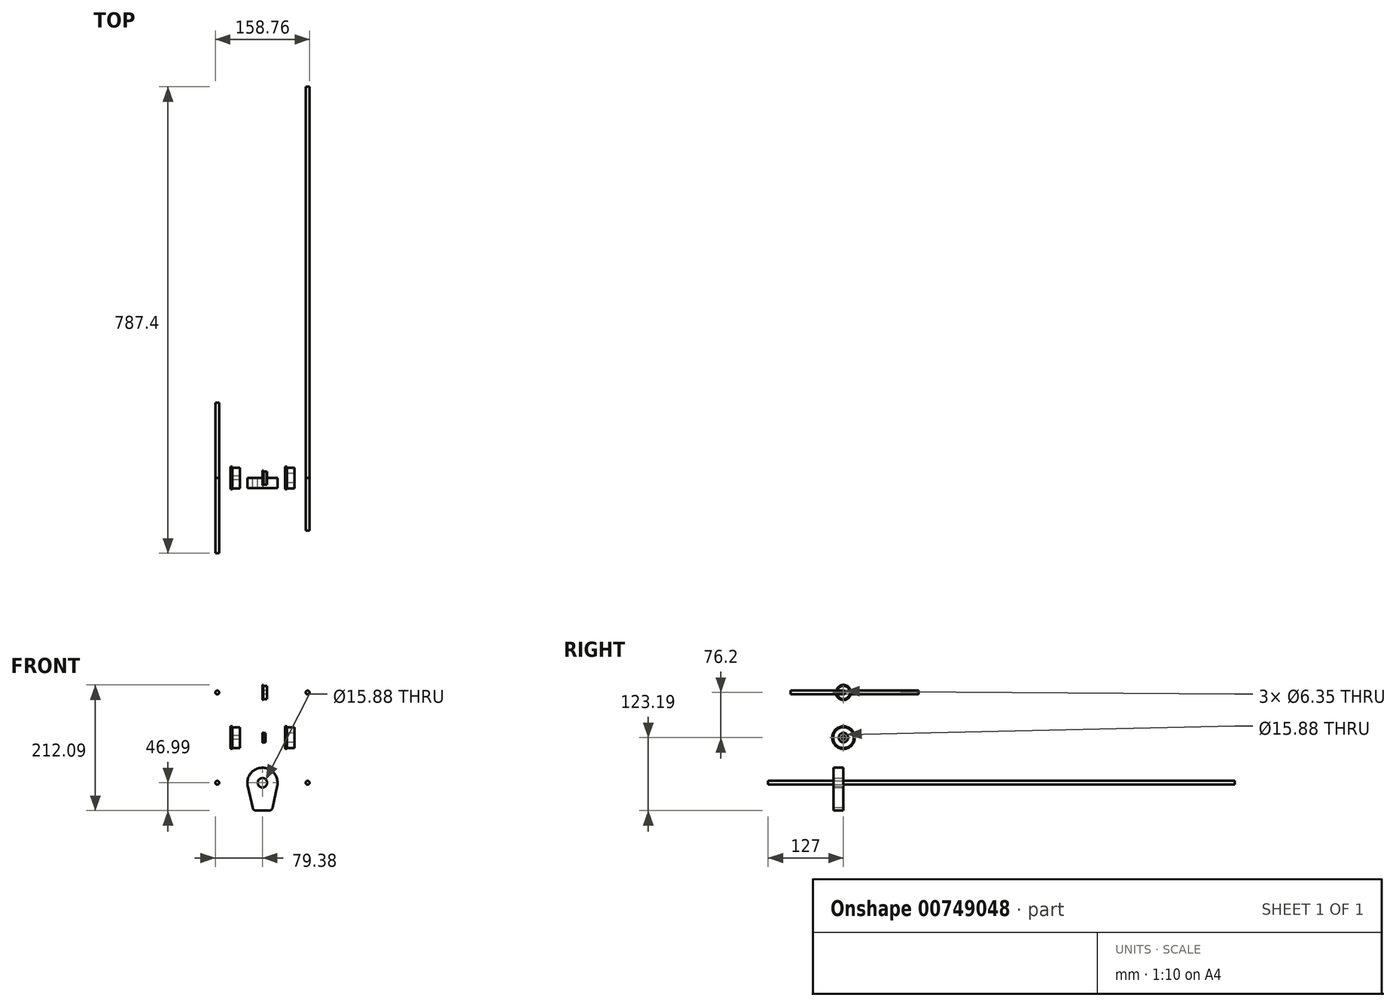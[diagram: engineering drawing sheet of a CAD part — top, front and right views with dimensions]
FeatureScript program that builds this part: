
annotation { "Feature Type Name" : "Feature", "Feature Type Description" : "" }
export const myFeature = defineFeature(function(context is Context, id is Id, definition is map)
    precondition{}
    {
        {
            var Q0;
            Q0=qCreatedBy(makeId("Front.planeOp"),FACE);
            var sketch = newSketch(context, id + "F0", { "sketchPlane" : qUnion([Q0])});
            skLineSegment(sketch, "E0", {"start": v(0, 3.17) * mm, "end": v(0, 8.76) * mm});
            skLineSegment(sketch, "E1", {"start": v(0, 8.76) * mm, "end": v(1.02, 8.76) * mm});
            skLineSegment(sketch, "E2", {"start": v(1.02, 8.76) * mm, "end": v(1.02, 7.94) * mm});
            skLineSegment(sketch, "E3", {"start": v(1.02, 7.94) * mm, "end": v(4.98, 7.94) * mm});
            skLineSegment(sketch, "E4", {"start": v(4.98, 7.94) * mm, "end": v(4.98, 3.18) * mm});
            skLineSegment(sketch, "E5", {"start": v(4.98, 3.17) * mm, "end": v(0, 3.17) * mm});
            skLineSegment(sketch, "E6", {"start": v(0, 0) * mm, "end": v(17.97, 0) * mm, "construction": true});
            skSolve(sketch);
        }
        {
            var Q0;
            Q0=makeQuery(id+"F0.imprint","IMPRINT",FACE,{"disambiguationData":[TD([[makeQuery(id+"F0.imprint","IMPRINT",EDGE,{"derivedFrom":sQuery(id+"F0.wireOp",EDGE,"E0")}),-1.0]])]});
            var Q1;
            Q1=sQuery(id+"F0.wireOp",EDGE,"E6");
            revolve(context, id + "F1", {"surfaceOperationType" : NewSurfaceOperationType.NEW, "entities" : qUnion([Q0]), "axis" : qUnion([Q1]), "revolveType" : RevolveType.FULL});
        }
        {
            var Q0;
            Q0=qCreatedBy(makeId("Front.planeOp"),FACE);
            var sketch = newSketch(context, id + "F2", { "sketchPlane" : qUnion([Q0])});
            skLineSegment(sketch, "E7", {"start": v(38.1, 7.94) * mm, "end": v(38.1, 19.05) * mm});
            skLineSegment(sketch, "E8", {"start": v(38.1, 19.05) * mm, "end": v(41.27, 19.05) * mm});
            skLineSegment(sketch, "E9", {"start": v(41.27, 19.05) * mm, "end": v(41.27, 17.46) * mm});
            skLineSegment(sketch, "E10", {"start": v(41.27, 17.46) * mm, "end": v(53.98, 17.46) * mm});
            skLineSegment(sketch, "E11", {"start": v(53.98, 17.46) * mm, "end": v(53.98, 7.94) * mm});
            skLineSegment(sketch, "E12", {"start": v(53.98, 7.94) * mm, "end": v(38.1, 7.94) * mm});
            skLineSegment(sketch, "E13", {"start": v(0, 0) * mm, "end": v(76.47, 0) * mm, "construction": true});
            skSolve(sketch);
        }
        {
            var Q0;
            Q0=makeQuery(id+"F2.imprint","IMPRINT",FACE,{"disambiguationData":[TD([[makeQuery(id+"F2.imprint","IMPRINT",EDGE,{"derivedFrom":sQuery(id+"F2.wireOp",EDGE,"E7")}),-1.0]])]});
            var Q1;
            Q1=sQuery(id+"F2.wireOp",EDGE,"E13");
            revolve(context, id + "F3", {"surfaceOperationType" : NewSurfaceOperationType.NEW, "entities" : qUnion([Q0]), "axis" : qUnion([Q1]), "revolveType" : RevolveType.FULL});
        }
        {
            var Q0;
            Q0=qCreatedBy(makeId("Front.planeOp"),FACE);
            var sketch = newSketch(context, id + "F4", { "sketchPlane" : qUnion([Q0])});
            skCircle(sketch, "E14", {"center": v(-76.2, 76.2) * mm, "radius": 3.18 * mm});
            skSolve(sketch);
        }
        {
            var Q0;
            Q0 = qSketchRegion(id + "F4", true);
            extrude(context, id + "F5", {"entities" : qUnion([Q0]), "oppositeDirection" : true, "depth" : 127 * mm, "offsetDistance" : 25.4 * mm});
        }
        {
            var Q0;
            Q0=qCreatedBy(makeId("Front.planeOp"),FACE);
            var sketch = newSketch(context, id + "F6", { "sketchPlane" : qUnion([Q0])});
            skCircle(sketch, "E15", {"center": v(76.2, 76.2) * mm, "radius": 3.18 * mm});
            skSolve(sketch);
        }
        {
            var Q0;
            Q0 = qSketchRegion(id + "F6", true);
            extrude(context, id + "F7", {"entities" : qUnion([Q0]), "depth" : 88.9 * mm, "offsetDistance" : 25.4 * mm});
        }
        {
            var Q0;
            Q0=qCreatedBy(makeId("Front.planeOp"),FACE);
            var sketch = newSketch(context, id + "F8", { "sketchPlane" : qUnion([Q0])});
            skCircle(sketch, "E16", {"center": v(-76.2, -76.2) * mm, "radius": 3.18 * mm});
            skSolve(sketch);
        }
        {
            var Q0;
            Q0 = qSketchRegion(id + "F8", true);
            extrude(context, id + "F9", {"entities" : qUnion([Q0]), "depth" : 127 * mm, "offsetDistance" : 25.4 * mm});
        }
        {
            var Q0;
            Q0=qCreatedBy(makeId("Front.planeOp"),FACE);
            var sketch = newSketch(context, id + "F10", { "sketchPlane" : qUnion([Q0])});
            skLineSegment(sketch, "E17", {"start": v(-53.98, 19.05) * mm, "end": v(-53.98, 3.18) * mm});
            skLineSegment(sketch, "E18", {"start": v(-53.98, 3.18) * mm, "end": v(-38.1, 3.18) * mm});
            skLineSegment(sketch, "E19", {"start": v(-38.1, 3.18) * mm, "end": v(-38.1, 17.46) * mm});
            skLineSegment(sketch, "E20", {"start": v(-38.1, 17.46) * mm, "end": v(-50.8, 17.46) * mm});
            skLineSegment(sketch, "E21", {"start": v(-50.8, 17.46) * mm, "end": v(-50.8, 19.05) * mm});
            skLineSegment(sketch, "E22", {"start": v(-50.8, 19.05) * mm, "end": v(-53.98, 19.05) * mm});
            skLineSegment(sketch, "E23", {"start": v(-59.24, 0) * mm, "end": v(-33.55, 0) * mm, "construction": true});
            skSolve(sketch);
        }
        {
            var Q0;
            Q0 = qSketchRegion(id + "F10", true);
            var Q1;
            Q1=sQuery(id+"F10.wireOp",EDGE,"E23");
            revolve(context, id + "F11", {"surfaceOperationType" : NewSurfaceOperationType.NEW, "entities" : qUnion([Q0]), "axis" : qUnion([Q1]), "revolveType" : RevolveType.FULL});
        }
        {
            var Q0;
            Q0=qCreatedBy(makeId("Front.planeOp"),FACE);
            var sketch = newSketch(context, id + "F12", { "sketchPlane" : qUnion([Q0])});
            skCircle(sketch, "E24", {"center": v(0, -76.2) * mm, "radius": 25.4 * mm});
            skLineSegment(sketch, "E25", {"start": v(-10.44, -123.2) * mm, "end": v(10.99, -123.2) * mm});
            skPoint(sketch, "E26.visualSharp", {"position": v(-15.6, -123.2) * mm});
            skArc(sketch, "E26.filletArc", {"start": v(-16.66, -118.14) * mm, "mid": v(-14.45, -121.77) * mm, "end": v(-10.44, -123.2) * mm});
            skPoint(sketch, "E27.visualSharp", {"position": v(16.15, -123.2) * mm});
            skArc(sketch, "E27.filletArc", {"start": v(10.99, -123.19) * mm, "mid": v(15, -121.77) * mm, "end": v(17.2, -118.14) * mm});
            skLineSegment(sketch, "E28", {"start": v(17.2, -118.14) * mm, "end": v(24.87, -81.38) * mm});
            skLineSegment(sketch, "E29", {"start": v(24.87, -81.38) * mm, "end": v(-24.87, -81.38) * mm, "construction": true});
            skLineSegment(sketch, "E30", {"start": v(-24.87, -81.38) * mm, "end": v(-16.66, -118.14) * mm});
            skCircle(sketch, "E31", {"center": v(0, -76.2) * mm, "radius": 7.94 * mm});
            skSolve(sketch);
        }
        {
            var Q0;
            Q0 = qSketchRegion(id + "F12", true);
            extrude(context, id + "F13", {"entities" : qUnion([Q0]), "depth" : 16.64 * mm, "offsetDistance" : 25.4 * mm});
        }
        {
            var Q0;
            Q0=qCreatedBy(makeId("Front.planeOp"),FACE);
            var sketch = newSketch(context, id + "F14", { "sketchPlane" : qUnion([Q0])});
            skLineSegment(sketch, "E32", {"start": v(-17.98, 76.2) * mm, "end": v(17.47, 76.2) * mm, "construction": true});
            skLineSegment(sketch, "E33", {"start": v(0, 88.9) * mm, "end": v(0, 79.38) * mm});
            skLineSegment(sketch, "E34", {"start": v(0, 79.38) * mm, "end": v(7.94, 79.38) * mm});
            skLineSegment(sketch, "E35", {"start": v(7.94, 79.38) * mm, "end": v(7.94, 87.31) * mm});
            skLineSegment(sketch, "E36", {"start": v(7.94, 87.31) * mm, "end": v(1.24, 87.31) * mm});
            skLineSegment(sketch, "E37", {"start": v(1.24, 87.31) * mm, "end": v(1.24, 88.9) * mm});
            skLineSegment(sketch, "E38", {"start": v(1.24, 88.9) * mm, "end": v(0, 88.9) * mm});
            skSolve(sketch);
        }
        {
            var Q0;
            Q0 = qSketchRegion(id + "F14", true);
            var Q1;
            Q1=sQuery(id+"F14.wireOp",EDGE,"E32");
            revolve(context, id + "F15", {"surfaceOperationType" : NewSurfaceOperationType.NEW, "entities" : qUnion([Q0]), "axis" : qUnion([Q1]), "revolveType" : RevolveType.FULL});
        }
        {
            var Q0;
            Q0=qCreatedBy(makeId("Front.planeOp"),FACE);
            var sketch = newSketch(context, id + "F16", { "sketchPlane" : qUnion([Q0])});
            skCircle(sketch, "E39", {"center": v(76.2, -76.2) * mm, "radius": 3.18 * mm});
            skSolve(sketch);
        }
        {
            var Q0;
            Q0 = qSketchRegion(id + "F16", true);
            extrude(context, id + "F17", {"entities" : qUnion([Q0]), "oppositeDirection" : true, "depth" : 660.4 * mm, "offsetDistance" : 25.4 * mm});
        }
    });
